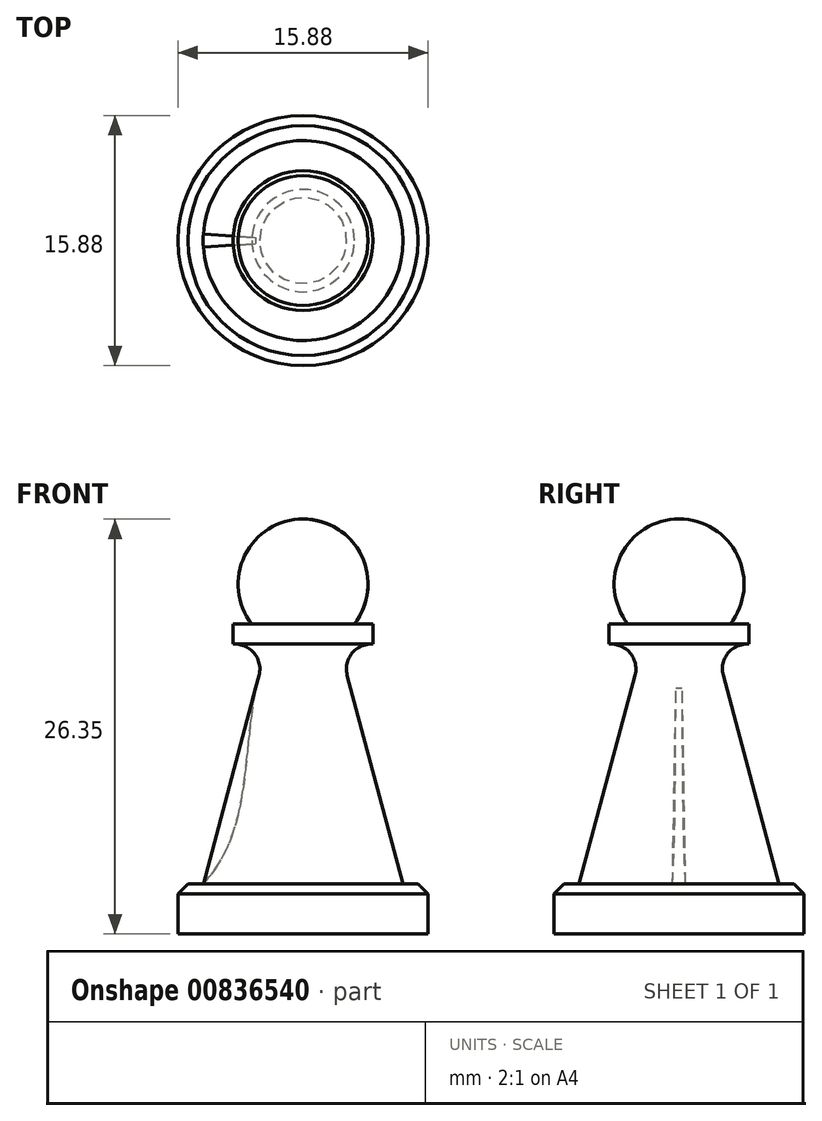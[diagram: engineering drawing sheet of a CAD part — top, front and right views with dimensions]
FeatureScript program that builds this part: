
annotation { "Feature Type Name" : "Feature", "Feature Type Description" : "" }
export const myFeature = defineFeature(function(context is Context, id is Id, definition is map)
    precondition{}
    {
        {
            var Q0;
            Q0=qCreatedBy(makeId("Top.planeOp"),FACE);
            var sketch = newSketch(context, id + "F0", { "sketchPlane" : qUnion([Q0])});
            skCircle(sketch, "E0", {"center": v(0, 0) * mm, "radius": 7.94 * mm});
            skSolve(sketch);
        }
        {
            var Q0;
            Q0 = qSketchRegion(id + "F0", true);
            extrude(context, id + "F1", {"entities" : qUnion([Q0]), "depth" : 3.17 * mm, "offsetDistance" : 25.4 * mm});
        }
        {
            var Q0;
            Q0=makeQuery(id+"F1.opExtrude","CAP_FACE",FACE,{"disambiguationData":[OSD([sQuery(id+"F0.wireOp",EDGE,"E0")])],"isStart":false});
            var sketch = newSketch(context, id + "F2", { "sketchPlane" : qUnion([Q0])});
            skCircle(sketch, "E1", {"center": v(0, 0) * mm, "radius": 6.35 * mm});
            skSolve(sketch);
        }
        {
            var Q0;
            Q0 = qSketchRegion(id + "F2", true);
            extrude(context, id + "F3", {"entities" : qUnion([Q0]), "operationType" : NewBodyOperationType.ADD, "depth" : 15.88 * mm, "offsetDistance" : 25.4 * mm, "hasDraft" : true, "draftAngle" : 15 * degree, "draftPullDirection" : true});
        }
        {
            var Q0;
            Q0=makeQuery(id+"F1.opExtrude","CAP_EDGE",EDGE,{"disambiguationData":[OSD([sQuery(id+"F0.wireOp",EDGE,"E0")])],"isStart":false});
            chamfer(context, id + "F4", {"entities" : qUnion([Q0]), "width" : 0.64 * mm, "tangentPropagation" : true});
        }
        {
            var Q0;
            Q0=qCreatedBy(makeId("Front.planeOp"),FACE);
            var sketch = newSketch(context, id + "F5", { "sketchPlane" : qUnion([Q0])});
            skLineSegment(sketch, "E2", {"start": v(-6.35, 3.17) * mm, "end": v(-3.01, 15.62) * mm});
            skLineSegment(sketch, "E3", {"start": v(0, 19.2) * mm, "end": v(0, 12.84) * mm});
            skFitSpline(sketch, "E4", {"points": [v(-6.35, 3.18) * mm, v(-3.01, 15.62) * mm], "startDerivative": vector(9.18, 9.9) * mm, "endDerivative": vector(2.57, 13.36) * mm});
            skLineSegment(sketch, "E5", {"start": v(-3.01, 15.62) * mm, "end": v(-6.35, 3.18) * mm});
            skSolve(sketch);
        }
        {
            var Q0;
            Q0 = qSketchRegion(id + "F5", true);
            var Q1;
            Q1=sQuery(id+"F5.wireOp",EDGE,"E3");
            revolve(context, id + "F6", {"operationType" : NewBodyOperationType.REMOVE, "surfaceOperationType" : NewSurfaceOperationType.NEW, "entities" : qUnion([Q0]), "axis" : qUnion([Q1]), "revolveType" : RevolveType.SYMMETRIC, "oppositeDirection" : true, "angle" : 7.5 * degree});
        }
        {
            var Q0;
            Q0=qCreatedBy(makeId("Front.planeOp"),FACE);
            var sketch = newSketch(context, id + "F7", { "sketchPlane" : qUnion([Q0])});
            skLineSegment(sketch, "E6", {"start": v(0, 19.05) * mm, "end": v(-2.1, 19.05) * mm});
            skPoint(sketch, "E7", {"position": v(0, 19.05) * mm});
            skPoint(sketch, "E8.orphan", {"position": v(2.1, 19.05) * mm});
            skLineSegment(sketch, "E9", {"start": v(-4.45, 18.41) * mm, "end": v(-4.45, 19.69) * mm});
            skLineSegment(sketch, "E10", {"start": v(-4.45, 19.69) * mm, "end": v(-3.25, 19.69) * mm});
            skLineSegment(sketch, "E11", {"start": v(-3.01, 15.62) * mm, "end": v(-2.8, 16.42) * mm});
            skLineSegment(sketch, "E12", {"start": v(-4.45, 18.41) * mm, "end": v(-4.34, 18.41) * mm});
            skArc(sketch, "E13", {"start": v(0, 26.35) * mm, "mid": v(-3.7, 24.04) * mm, "end": v(-3.25, 19.69) * mm});
            skPoint(sketch, "E14", {"position": v(-3.25, 19.69) * mm});
            skPoint(sketch, "E15.orphan", {"position": v(0, 19.69) * mm});
            skLineSegment(sketch, "E16", {"start": v(0, 19.05) * mm, "end": v(0, 26.35) * mm});
            skPoint(sketch, "E17.newPointB", {"position": v(-2.1, 19.05) * mm});
            skArc(sketch, "E17.filletArc", {"start": v(-2.8, 16.42) * mm, "mid": v(-3.08, 17.8) * mm, "end": v(-4.34, 18.41) * mm});
            skLineSegment(sketch, "E18", {"start": v(-2.1, 19.05) * mm, "end": v(-2.8, 16.42) * mm});
            skPoint(sketch, "E19.end.orphan", {"position": v(3.01, 15.62) * mm});
            skSolve(sketch);
        }
        {
            var Q0;
            Q0 = qSketchRegion(id + "F7", true);
            var Q1;
            Q1=sQuery(id+"F7.wireOp",EDGE,"E16");
            revolve(context, id + "F8", {"operationType" : NewBodyOperationType.ADD, "surfaceOperationType" : NewSurfaceOperationType.NEW, "entities" : qUnion([Q0]), "axis" : qUnion([Q1]), "revolveType" : RevolveType.FULL});
        }
    });
